# Revit family: Gymnasium-Eqpt_Basketball_IPIbybison_IP1370FF
name_source: partatom
category: Specialty Equipment
revit_build: Autodesk Revit 2018 (Build: 20170927_1515(x64)
units: mm (PartAtom-declared; Revit-internal decimal feet)

## family parameters
Always vertical = Yes
Cut with Voids When Loaded = No
OmniClass Number = 23.40.50.34.14
OmniClass Title = Gymnasium Equipment
Part Type = Normal
Room Calculation Point = No
Round Connector Dimension = Use Diameter
Shared = No

## types (1)
- Front Fold Offset Y- Front Braced
    Assembly Code = E1090
    Available Options = as Specified
    Backboard Type = Backboard_BA42XLGlass
    Description = IPI by Bison Front Folding Basketball Frame and Backboard - IP1345FRBF 23' as Specified
    Expected Lifespan (Years) = 0
    Maintenance Schedule (Months) = 0
    Manufacturer = IPI by Bison
    Manufacturer Fax = 800-638-0698
    Manufacturer Website = https://ipibybison.com
    Model = IP1370FF 23'
    Product Data = http://www.arcat.com
    Revision = R0_04-2018
    Sales Information = https://ipibybison.com
    URL = https://ipibybison.com
    Warranty Duration (Years) = 0

## geometry (parser evidence)
native form markers: Sweep x4
no freeform markers — native parametric forms only
